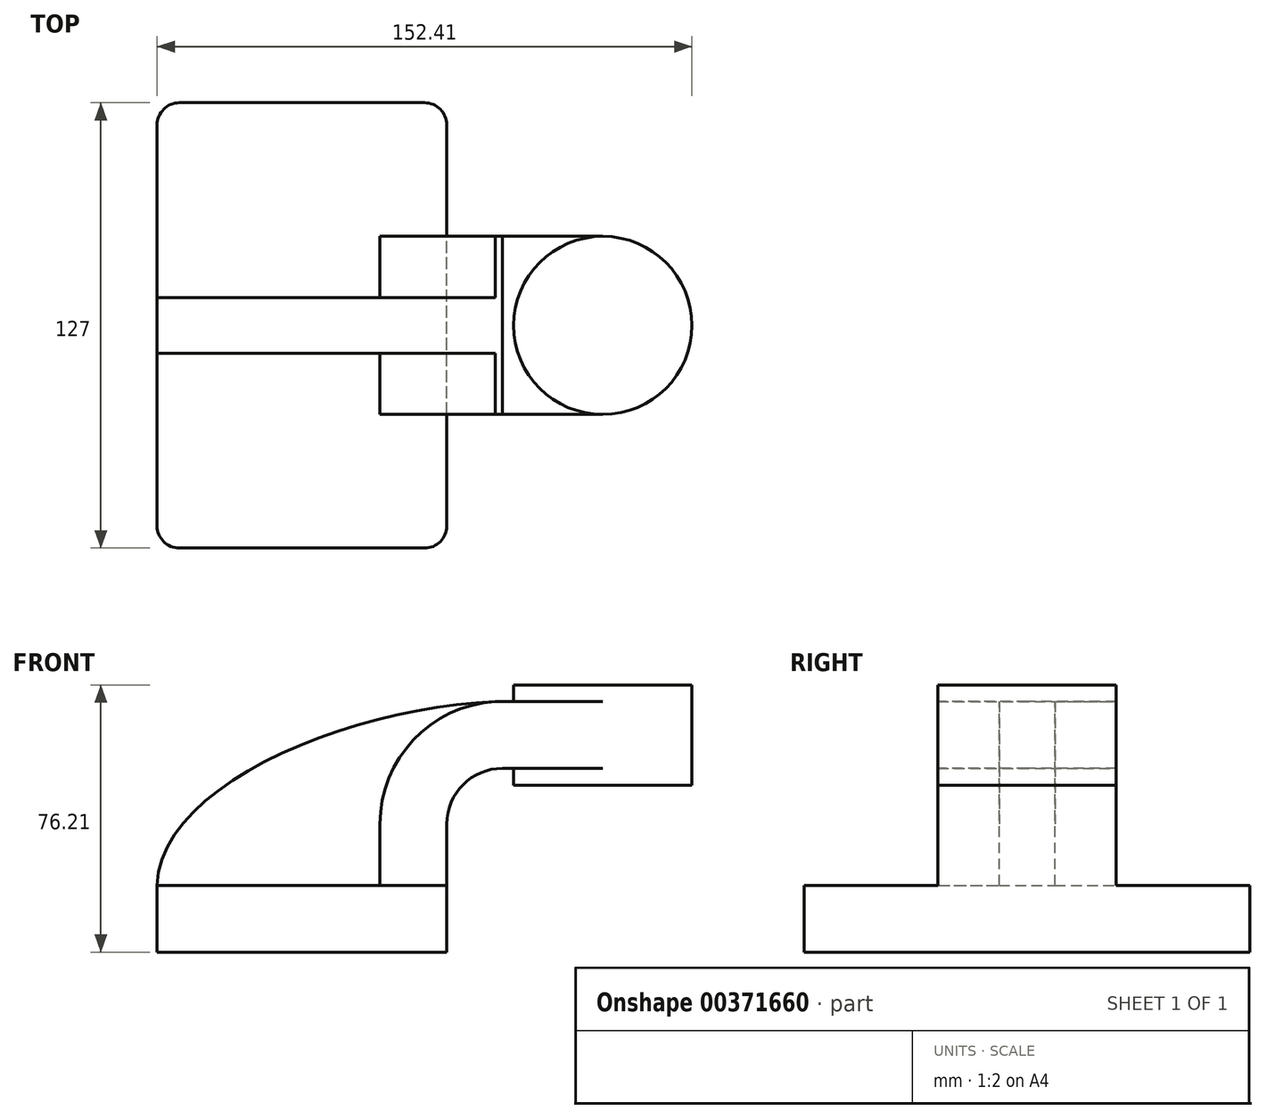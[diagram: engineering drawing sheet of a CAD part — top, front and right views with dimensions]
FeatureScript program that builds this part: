
annotation { "Feature Type Name" : "Feature", "Feature Type Description" : "" }
export const myFeature = defineFeature(function(context is Context, id is Id, definition is map)
    precondition{}
    {
        {
            var Q0;
            Q0=qCreatedBy(makeId("Front.planeOp"),FACE);
            var sketch = newSketch(context, id + "F0", { "sketchPlane" : qUnion([Q0])});
            skLineSegment(sketch, "E0.bottom", {"start": v(-41.28, -9.53) * mm, "end": v(41.28, -9.53) * mm});
            skLineSegment(sketch, "E0.top", {"start": v(-41.28, 9.53) * mm, "end": v(41.28, 9.53) * mm});
            skLineSegment(sketch, "E0.left", {"start": v(-41.28, -9.53) * mm, "end": v(-41.28, 9.53) * mm});
            skLineSegment(sketch, "E0.right", {"start": v(41.28, -9.53) * mm, "end": v(41.28, 9.53) * mm});
            skPoint(sketch, "E0.middle", {"position": v(0, 0) * mm});
            skLineSegment(sketch, "E1.bottom", {"start": v(60.33, 38.1) * mm, "end": v(111.12, 38.1) * mm});
            skLineSegment(sketch, "E1.top", {"start": v(60.33, 66.68) * mm, "end": v(111.12, 66.68) * mm});
            skLineSegment(sketch, "E1.right", {"start": v(111.12, 38.1) * mm, "end": v(111.12, 66.68) * mm});
            skPoint(sketch, "E1.middle", {"position": v(85.72, 52.39) * mm});
            skLineSegment(sketch, "E2", {"start": v(41.28, 9.53) * mm, "end": v(41.28, 27) * mm});
            skArc(sketch, "E3", {"start": v(41.27, 27) * mm, "mid": v(45.92, 38.23) * mm, "end": v(57.15, 42.88) * mm});
            skPoint(sketch, "E4.endSnap0", {"position": v(85.73, 38.1) * mm});
            skPoint(sketch, "E4.end.orphan", {"position": v(85.73, 42.88) * mm});
            skLineSegment(sketch, "E5", {"start": v(60.33, 66.68) * mm, "end": v(60.33, 38.1) * mm});
            skLineSegment(sketch, "E6", {"start": v(57.15, 42.88) * mm, "end": v(85.73, 42.88) * mm});
            skLineSegment(sketch, "E7.0", {"start": v(57.15, 61.93) * mm, "end": v(85.73, 61.93) * mm});
            skArc(sketch, "E7.1", {"start": v(22.22, 27) * mm, "mid": v(32.45, 51.7) * mm, "end": v(57.15, 61.93) * mm});
            skLineSegment(sketch, "E7.2", {"start": v(22.22, 9.53) * mm, "end": v(22.22, 27) * mm});
            skLineSegment(sketch, "E8", {"start": v(85.73, 38.1) * mm, "end": v(85.72, 66.68) * mm});
            skFitSpline(sketch, "E9", {"points": [v(-41.28, 9.53) * mm, v(57.15, 61.93) * mm], "startDerivative": vector(2.4, 88.06) * mm, "endDerivative": vector(124.55, 2.62) * mm});
            skSolve(sketch);
        }
        {
            var Q0;
            Q0=makeQuery(id+"F0.imprint","IMPRINT",FACE,{"disambiguationData":[TD([[makeQuery(id+"F0.imprint","IMPRINT",EDGE,{"derivedFrom":sQuery(id+"F0.wireOp",EDGE,"E0.bottom")}),1.0]])]});
            extrude(context, id + "F1", {"entities" : qUnion([Q0]), "endBound" : BoundingType.SYMMETRIC, "depth" : 127 * mm});
        }
        {
            var Q0;
            {var subQ5=sQuery(id+"F0.wireOp",EDGE,"E2");Q0=makeQuery(id+"F0.imprint","IMPRINT",FACE,{"disambiguationData":[TD([[makeQuery(id+"F0.imprint","IMPRINT",EDGE,{"derivedFrom":subQ5}),1.0]])]});}
            var Q1;
            {var subQ0=sQuery(id+"F0.wireOp",EDGE,"E7.0");var subQ1=sQuery(id+"F0.wireOp",EDGE,"E5");var subQ2=makeQuery(id+"F0.imprint","INTERSECT",VERTEX,{"derivedFrom":[subQ1,subQ0]});Q1=makeQuery(id+"F0.imprint","IMPRINT",FACE,{"disambiguationData":[TD([[makeQuery(id+"F0.imprint","IMPRINT",EDGE,{"disambiguationData":[TD([[subQ2,-1.0]])],"derivedFrom":subQ1}),1.0]])]});}
            extrude(context, id + "F2", {"entities" : qUnion([Q0, Q1]), "operationType" : NewBodyOperationType.ADD, "endBound" : BoundingType.SYMMETRIC, "depth" : 50.8 * mm});
        }
        {
            var Q0;
            {var subQ3=sQuery(id+"F0.wireOp",EDGE,"E7.2");Q0=makeQuery(id+"F0.imprint","IMPRINT",FACE,{"disambiguationData":[TD([[makeQuery(id+"F0.imprint","IMPRINT",EDGE,{"derivedFrom":subQ3}),1.0]])]});}
            extrude(context, id + "F3", {"entities" : qUnion([Q0]), "operationType" : NewBodyOperationType.ADD, "endBound" : BoundingType.SYMMETRIC, "depth" : 15.88 * mm});
        }
        {
            var Q0;
            {var subQ4=sQuery(id+"F0.wireOp",EDGE,"E1.right");Q0=makeQuery(id+"F0.imprint","IMPRINT",FACE,{"disambiguationData":[TD([[makeQuery(id+"F0.imprint","IMPRINT",EDGE,{"derivedFrom":subQ4}),1.0]])]});}
            var Q1;
            Q1=sQuery(id+"F0.wireOp",EDGE,"E8");
            var Q2;
            Q2=sQuery(id+"F0.wireOp",EDGE,"E8");
            revolve(context, id + "F4", {"operationType" : NewBodyOperationType.ADD, "entities" : qUnion([Q0]), "surfaceEntities" : qUnion([Q1]), "axis" : qUnion([Q2]), "revolveType" : RevolveType.FULL});
        }
        {
            var Q0;
            Q0=makeQuery(id+"F1.opExtrude","CAP_EDGE",EDGE,{"disambiguationData":[OSD([sQuery(id+"F0.wireOp",EDGE,"E0.right")])],"isStart":false});
            var Q1;
            Q1=makeQuery(id+"F1.opExtrude","CAP_EDGE",EDGE,{"disambiguationData":[OSD([sQuery(id+"F0.wireOp",EDGE,"E0.left")])],"isStart":false});
            var Q2;
            Q2=makeQuery(id+"F1.opExtrude","CAP_EDGE",EDGE,{"disambiguationData":[OSD([sQuery(id+"F0.wireOp",EDGE,"E0.right")])],"isStart":true});
            var Q3;
            Q3=makeQuery(id+"F1.opExtrude","CAP_EDGE",EDGE,{"disambiguationData":[OSD([sQuery(id+"F0.wireOp",EDGE,"E0.left")])],"isStart":true});
            fillet(context, id + "F5", {"entities" : qUnion([Q0, Q1, Q2, Q3]), "radius" : 6.35 * mm, "tangentPropagation" : true, "allowEdgeOverflow" : false});
        }
    });
